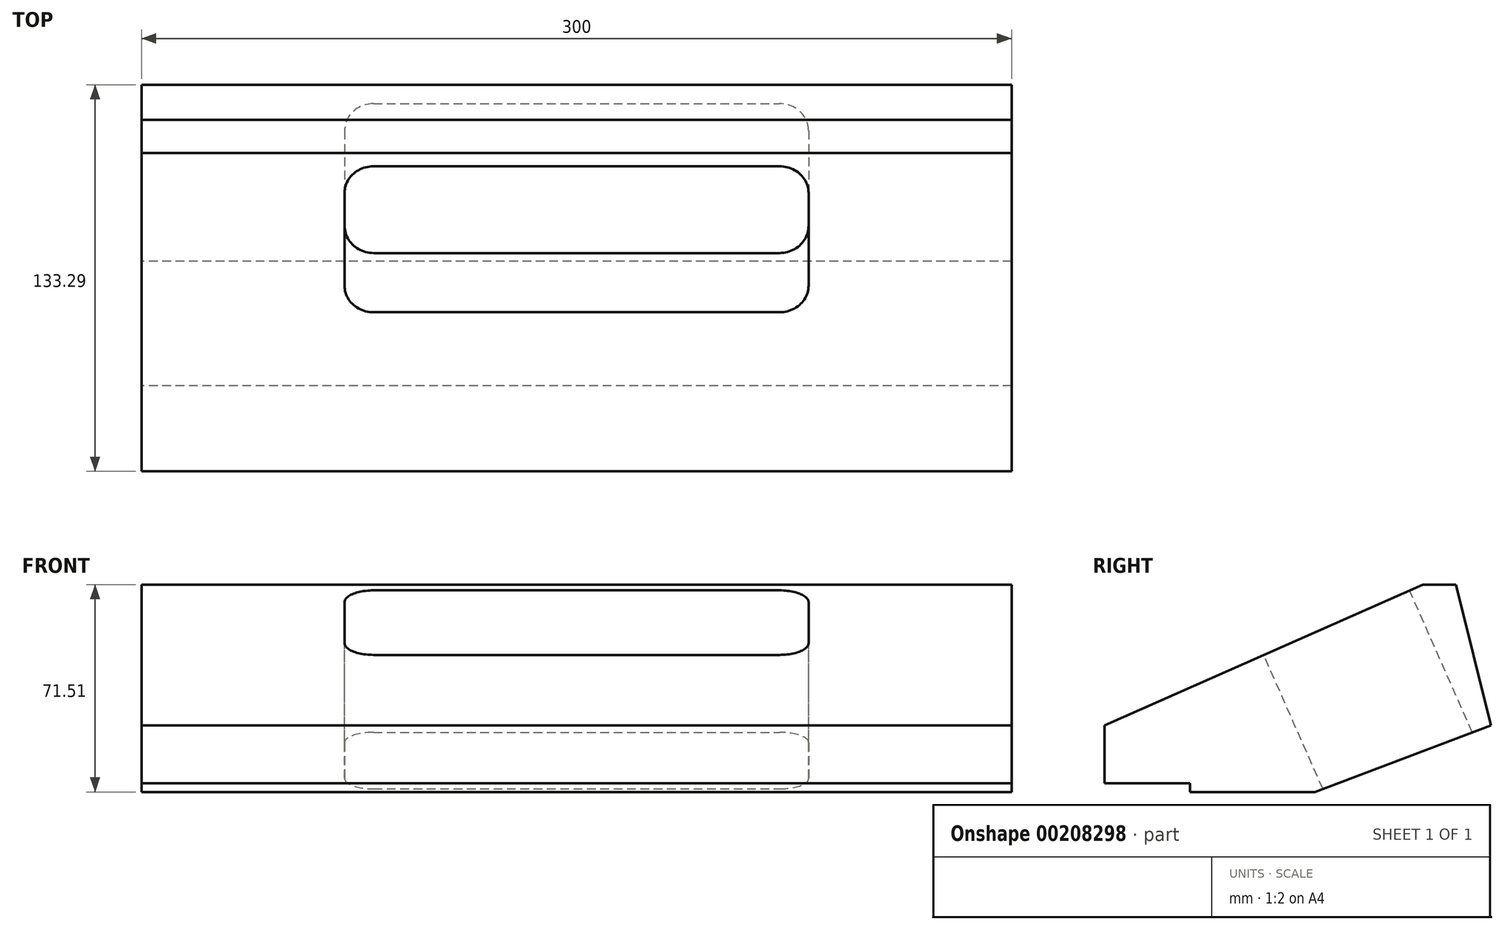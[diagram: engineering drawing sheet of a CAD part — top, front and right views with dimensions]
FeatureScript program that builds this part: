
annotation { "Feature Type Name" : "Feature", "Feature Type Description" : "" }
export const myFeature = defineFeature(function(context is Context, id is Id, definition is map)
    precondition{}
    {
        {
            var Q0;
            Q0=qCreatedBy(makeId("Right.planeOp"),FACE);
            var sketch = newSketch(context, id + "F0", { "sketchPlane" : qUnion([Q0])});
            skLineSegment(sketch, "E0", {"start": v(0, -20) * mm, "end": v(29.5, -20) * mm});
            skLineSegment(sketch, "E1", {"start": v(29.5, -20) * mm, "end": v(29.5, -23) * mm});
            skLineSegment(sketch, "E2", {"start": v(29.5, -23) * mm, "end": v(72.5, -23) * mm});
            skLineSegment(sketch, "E3", {"start": v(72.5, -23) * mm, "end": v(133.3, 0) * mm});
            skLineSegment(sketch, "E4", {"start": v(133.3, 0) * mm, "end": v(121.2, 48.51) * mm});
            skLineSegment(sketch, "E5", {"start": v(121.2, 48.51) * mm, "end": v(109.76, 48.51) * mm});
            skLineSegment(sketch, "E6", {"start": v(109.76, 48.51) * mm, "end": v(0, 0) * mm});
            skLineSegment(sketch, "E7", {"start": v(0, 0) * mm, "end": v(0, -20) * mm});
            skSolve(sketch);
        }
        {
            var Q0;
            Q0 = qSketchRegion(id + "F0", true);
            extrude(context, id + "F1", {"entities" : qUnion([Q0]), "depth" : 300 * mm});
        }
        {
            var Q0;
            Q0=makeQuery(id+"F1.opExtrude","SWEPT_FACE",FACE,{"disambiguationData":[OSD([sQuery(id+"F0.wireOp",EDGE,"E6")])]});
            var sketch = newSketch(context, id + "F2", { "sketchPlane" : qUnion([Q0])});
            skLineSegment(sketch, "E8.bottom", {"start": v(80, 115) * mm, "end": v(220, 115) * mm});
            skLineSegment(sketch, "E8.top", {"start": v(80, 60) * mm, "end": v(220, 60) * mm});
            skLineSegment(sketch, "E8.left", {"start": v(70, 105) * mm, "end": v(70, 70) * mm});
            skLineSegment(sketch, "E8.right", {"start": v(230, 105) * mm, "end": v(230, 70) * mm});
            skPoint(sketch, "E9.visualSharp", {"position": v(70, 60) * mm});
            skArc(sketch, "E9.filletArc", {"start": v(70, 70) * mm, "mid": v(72.93, 62.93) * mm, "end": v(80, 60) * mm});
            skPoint(sketch, "E10.visualSharp", {"position": v(70, 115) * mm});
            skArc(sketch, "E10.filletArc", {"start": v(80, 115) * mm, "mid": v(72.93, 112.07) * mm, "end": v(70, 105) * mm});
            skPoint(sketch, "E11.visualSharp", {"position": v(230, 115) * mm});
            skArc(sketch, "E11.filletArc", {"start": v(230, 105) * mm, "mid": v(227.07, 112.07) * mm, "end": v(220, 115) * mm});
            skPoint(sketch, "E12.visualSharp", {"position": v(230, 60) * mm});
            skArc(sketch, "E12.filletArc", {"start": v(220, 60) * mm, "mid": v(227.07, 62.93) * mm, "end": v(230, 70) * mm});
            skSolve(sketch);
        }
        {
            var Q0;
            Q0=makeQuery(id+"F2.imprint","IMPRINT",FACE,{"disambiguationData":[TD([[makeQuery(id+"F2.imprint","IMPRINT",EDGE,{"derivedFrom":sQuery(id+"F2.wireOp",EDGE,"E8.bottom")}),-1.0]])]});
            extrude(context, id + "F3", {"entities" : qUnion([Q0]), "operationType" : NewBodyOperationType.REMOVE, "oppositeDirection" : true, "depth" : 106 * mm});
        }
    });
